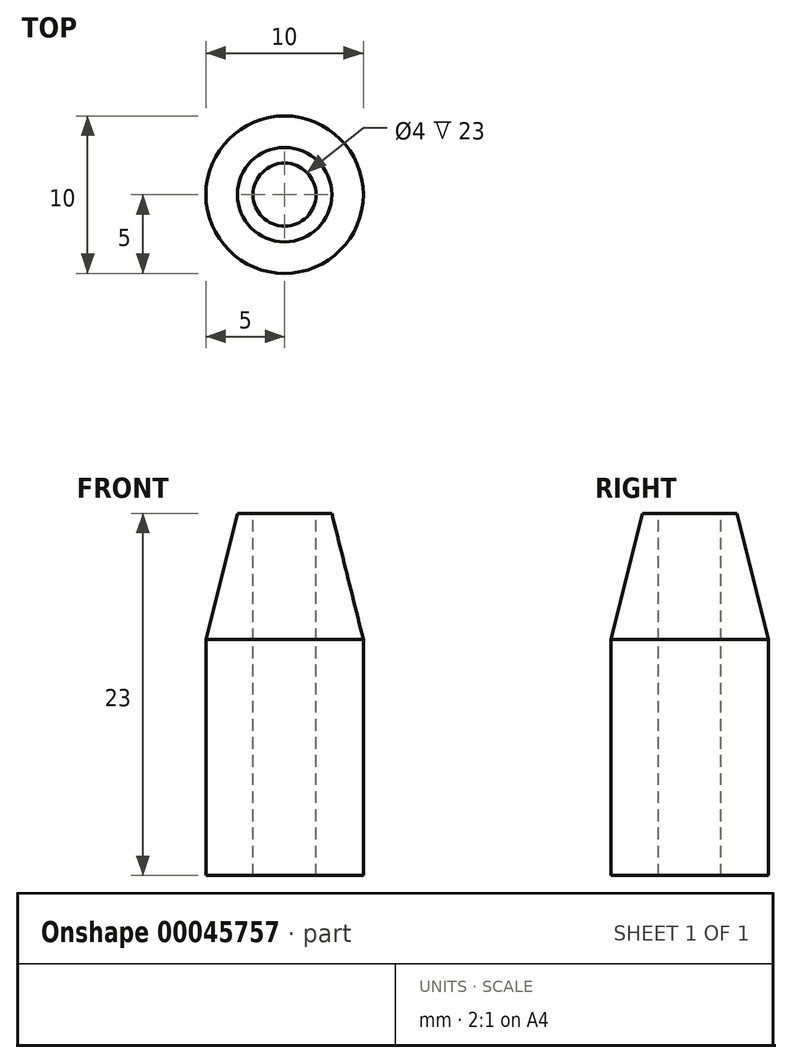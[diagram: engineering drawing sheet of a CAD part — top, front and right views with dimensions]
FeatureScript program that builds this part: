
annotation { "Feature Type Name" : "Feature", "Feature Type Description" : "" }
export const myFeature = defineFeature(function(context is Context, id is Id, definition is map)
    precondition{}
    {
        {
            var Q0;
            Q0=qCreatedBy(makeId("Front.planeOp"),FACE);
            var sketch = newSketch(context, id + "F0", { "sketchPlane" : qUnion([Q0])});
            skLineSegment(sketch, "E0.bottom", {"start": v(2, 0) * mm, "end": v(5, 0) * mm});
            skLineSegment(sketch, "E0.top", {"start": v(2, 15) * mm, "end": v(5, 15) * mm});
            skLineSegment(sketch, "E0.left", {"start": v(2, 0) * mm, "end": v(2, 15) * mm});
            skLineSegment(sketch, "E0.right", {"start": v(5, 0) * mm, "end": v(5, 15) * mm});
            skLineSegment(sketch, "E1.bottom", {"start": v(5, 15) * mm, "end": v(2, 15) * mm});
            skLineSegment(sketch, "E1.top", {"start": v(3, 23) * mm, "end": v(2, 23) * mm});
            skLineSegment(sketch, "E1.left", {"start": v(5, 15) * mm, "end": v(3, 23) * mm});
            skLineSegment(sketch, "E1.right", {"start": v(2, 15) * mm, "end": v(2, 23) * mm});
            skLineSegment(sketch, "E2", {"start": v(0, 23) * mm, "end": v(0, 0) * mm});
            skSolve(sketch);
        }
        {
            var Q0;
            Q0 = qSketchRegion(id + "F0", true);
            var Q1;
            Q1=sQuery(id+"F0.wireOp",EDGE,"E2");
            revolve(context, id + "F1", {"entities" : qUnion([Q0]), "axis" : qUnion([Q1]), "revolveType" : RevolveType.FULL});
        }
    });
